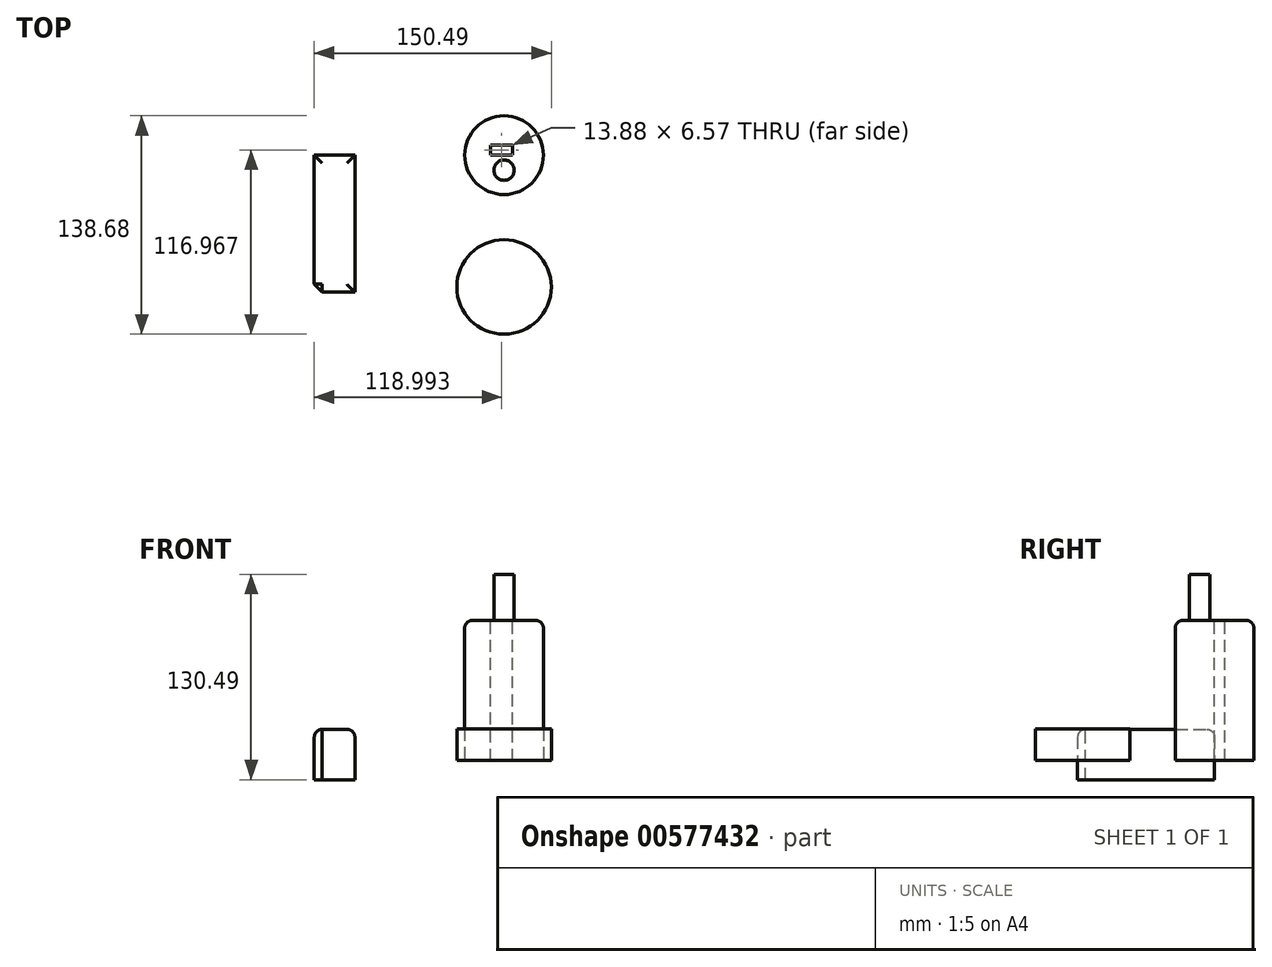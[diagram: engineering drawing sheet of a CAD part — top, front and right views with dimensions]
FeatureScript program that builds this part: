
annotation { "Feature Type Name" : "Feature", "Feature Type Description" : "" }
export const myFeature = defineFeature(function(context is Context, id is Id, definition is map)
    precondition{}
    {
        {
            var Q0;
            Q0=qCreatedBy(makeId("Top.planeOp"),FACE);
            var sketch = newSketch(context, id + "F0", { "sketchPlane" : qUnion([Q0])});
            skCircle(sketch, "E0", {"center": v(0, 0) * mm, "radius": 25 * mm});
            skSolve(sketch);
        }
        {
            var Q0;
            Q0 = qSketchRegion(id + "F0", true);
            extrude(context, id + "F1", {"entities" : qUnion([Q0]), "depth" : 89 * mm, "offsetDistance" : 25 * mm});
        }
        {
            var Q0;
            Q0=makeQuery(id+"F1.opExtrude","CAP_FACE",FACE,{"disambiguationData":[OSD([sQuery(id+"F0.wireOp",EDGE,"E0")])],"isStart":false});
            var sketch = newSketch(context, id + "F2", { "sketchPlane" : qUnion([Q0])});
            skLineSegment(sketch, "E1.bottom", {"start": v(-8.43, 0) * mm, "end": v(5.44, 0) * mm});
            skLineSegment(sketch, "E1.top", {"start": v(-8.43, 6.57) * mm, "end": v(5.44, 6.57) * mm});
            skLineSegment(sketch, "E1.left", {"start": v(-8.43, 0) * mm, "end": v(-8.43, 6.57) * mm});
            skLineSegment(sketch, "E1.right", {"start": v(5.44, 0) * mm, "end": v(5.44, 6.57) * mm});
            skSolve(sketch);
        }
        {
            var Q0;
            Q0 = qSketchRegion(id + "F2", true);
            extrude(context, id + "F3", {"entities" : qUnion([Q0]), "operationType" : NewBodyOperationType.REMOVE, "endBound" : BoundingType.UP_TO_NEXT, "oppositeDirection" : true, "depth" : 69.2 * mm, "offsetDistance" : 25 * mm});
        }
        {
            var Q0;
            Q0=makeQuery(id+"F1.opExtrude","CAP_FACE",FACE,{"disambiguationData":[OSD([sQuery(id+"F0.wireOp",EDGE,"E0")])],"isStart":false});
            var sketch = newSketch(context, id + "F4", { "sketchPlane" : qUnion([Q0])});
            skCircle(sketch, "E2", {"center": v(0, -9.53) * mm, "radius": 6.45 * mm});
            skSolve(sketch);
        }
        {
            var Q0;
            Q0 = qSketchRegion(id + "F4", true);
            extrude(context, id + "F5", {"entities" : qUnion([Q0]), "operationType" : NewBodyOperationType.ADD, "depth" : 29.3 * mm, "offsetDistance" : 25 * mm});
        }
        {
            var Q0;
            Q0=makeQuery(id+"F1.opExtrude","CAP_EDGE",EDGE,{"disambiguationData":[OSD([sQuery(id+"F0.wireOp",EDGE,"E0")])],"isStart":false});
            fillet(context, id + "F6", {"entities" : qUnion([Q0]), "radius" : 5 * mm, "tangentPropagation" : true, "allowEdgeOverflow" : false});
        }
        {
            var Q0;
            Q0=qCreatedBy(makeId("Top.planeOp"),FACE);
            var sketch = newSketch(context, id + "F7", { "sketchPlane" : qUnion([Q0])});
            skCircle(sketch, "E3", {"center": v(0, -83.68) * mm, "radius": 30 * mm});
            skSolve(sketch);
        }
        {
            var Q0;
            Q0 = qSketchRegion(id + "F7", true);
            extrude(context, id + "F8", {"entities" : qUnion([Q0]), "depth" : 20 * mm, "offsetDistance" : 25 * mm});
        }
        {
            var Q0;
            Q0=qCreatedBy(makeId("Front.planeOp"),FACE);
            var sketch = newSketch(context, id + "F9", { "sketchPlane" : qUnion([Q0])});
            skLineSegment(sketch, "E4.bottom", {"start": v(-120.49, 19.83) * mm, "end": v(-94.73, 19.83) * mm});
            skLineSegment(sketch, "E4.top", {"start": v(-120.49, -12.2) * mm, "end": v(-94.73, -12.2) * mm});
            skLineSegment(sketch, "E4.left", {"start": v(-120.49, 19.83) * mm, "end": v(-120.49, -12.2) * mm});
            skLineSegment(sketch, "E4.right", {"start": v(-94.73, 19.83) * mm, "end": v(-94.73, -12.2) * mm});
            skSolve(sketch);
        }
        {
            var Q0;
            Q0 = qSketchRegion(id + "F9", true);
            extrude(context, id + "F10", {"entities" : qUnion([Q0]), "depth" : 87 * mm, "offsetDistance" : 25 * mm});
        }
        {
            var Q0;
            Q0=makeQuery(id+"F10.opExtrude","SWEPT_FACE",FACE,{"disambiguationData":[OSD([sQuery(id+"F9.wireOp",EDGE,"E4.bottom")])]});
            fillet(context, id + "F11", {"entities" : qUnion([Q0]), "radius" : 5 * mm, "tangentPropagation" : true, "allowEdgeOverflow" : false});
        }
        {
            var Q0;
            Q0=makeQuery(id+"F10.opExtrude","CAP_EDGE",EDGE,{"disambiguationData":[OSD([sQuery(id+"F9.wireOp",EDGE,"E4.left")])],"isStart":false});
            chamfer(context, id + "F12", {"entities" : qUnion([Q0]), "width" : 5 * mm, "tangentPropagation" : true});
        }
    });
